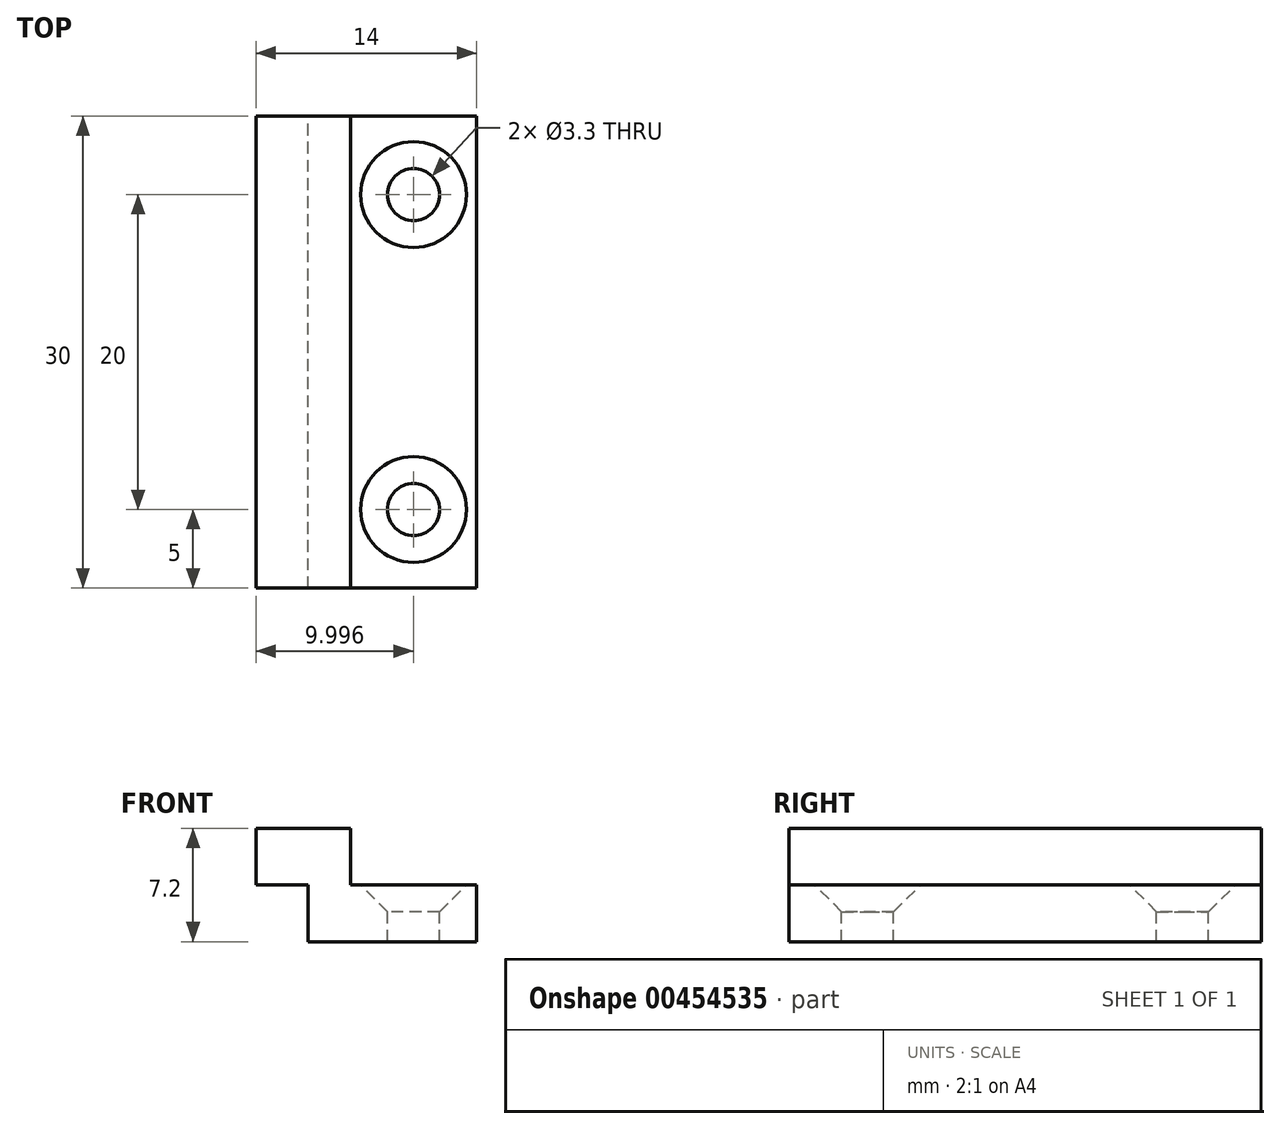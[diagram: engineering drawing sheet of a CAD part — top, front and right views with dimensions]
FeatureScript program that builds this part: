
annotation { "Feature Type Name" : "Feature", "Feature Type Description" : "" }
export const myFeature = defineFeature(function(context is Context, id is Id, definition is map)
    precondition{}
    {
        {
            var Q0;
            Q0=qCreatedBy(makeId("Front.planeOp"),FACE);
            var sketch = newSketch(context, id + "F0", { "sketchPlane" : qUnion([Q0])});
            skLineSegment(sketch, "E0", {"start": v(5.99, 0) * mm, "end": v(-4.71, 0) * mm});
            skLineSegment(sketch, "E1", {"start": v(-4.71, 0) * mm, "end": v(-4.71, 3.6) * mm});
            skLineSegment(sketch, "E2", {"start": v(-4.71, 3.6) * mm, "end": v(-8.01, 3.6) * mm});
            skLineSegment(sketch, "E3", {"start": v(-8.01, 3.6) * mm, "end": v(-8.01, 7.2) * mm});
            skLineSegment(sketch, "E4", {"start": v(-8.01, 7.2) * mm, "end": v(-2.01, 7.2) * mm});
            skLineSegment(sketch, "E5", {"start": v(-2.01, 7.2) * mm, "end": v(-2.01, 3.6) * mm});
            skLineSegment(sketch, "E6", {"start": v(-2.01, 3.6) * mm, "end": v(5.99, 3.6) * mm});
            skLineSegment(sketch, "E7", {"start": v(5.99, 3.6) * mm, "end": v(5.99, 0) * mm});
            skSolve(sketch);
        }
        {
            var Q0;
            Q0=makeQuery(id+"F0.imprint","IMPRINT",FACE,{"disambiguationData":[TD([[makeQuery(id+"F0.imprint","IMPRINT",EDGE,{"derivedFrom":sQuery(id+"F0.wireOp",EDGE,"E0")}),-1.0]])]});
            extrude(context, id + "F1", {"entities" : qUnion([Q0]), "depth" : 30 * mm});
        }
        {
            var Q0;
            Q0=makeQuery(id+"F1.opExtrude","SWEPT_FACE",FACE,{"disambiguationData":[OSD([sQuery(id+"F0.wireOp",EDGE,"E6")])]});
            var sketch = newSketch(context, id + "F2", { "sketchPlane" : qUnion([Q0])});
            skLineSegment(sketch, "E8", {"start": v(1.99, 0) * mm, "end": v(1.99, -30) * mm, "construction": true});
            skPoint(sketch, "E9", {"position": v(1.99, -5) * mm});
            skPoint(sketch, "E10", {"position": v(1.99, -25) * mm});
            skSolve(sketch);
        }
        {
            var Q0;
            Q0=sQuery(id+"F2.wireOp",VERTEX,"E9");
            var Q1;
            Q1=sQuery(id+"F2.wireOp",VERTEX,"E10");
            var Q2;
            Q2=makeQuery(id+"F1.opExtrude","SWEPT_BODY",BODY,{"disambiguationData":[OSD([sQuery(id+"F0.wireOp",EDGE,"E0"),sQuery(id+"F0.wireOp",EDGE,"E1"),sQuery(id+"F0.wireOp",EDGE,"E2"),sQuery(id+"F0.wireOp",EDGE,"E3"),sQuery(id+"F0.wireOp",EDGE,"E4"),sQuery(id+"F0.wireOp",EDGE,"E5"),sQuery(id+"F0.wireOp",EDGE,"E6"),sQuery(id+"F0.wireOp",EDGE,"E7")])]});
            hole(context, id + "F3", {"style" : HoleStyle.C_SINK, "endStyle" : HoleEndStyle.THROUGH, "standardTappedOrClearance" : lookupTablePath({ "standard" : "ISO", "fit" : "Normal", "size" : "M3", "type" : "Clearance" }), "standardBlindInLast" : lookupTablePath({ "fit" : "Standard", "standard" : "ISO", "size" : "M3", "type" : "Clearance" }), "holeDiameter" : 3.3 * mm, "cSinkDiameter" : 6.72 * mm, "cSinkAngle" : 90 * degree, "isTappedThrough" : true, "tappedDepth" : 12 * mm, "tapClearance" : 3, "locations" : qUnion([Q0, Q1]), "scope" : qUnion([Q2])});
        }
    });
